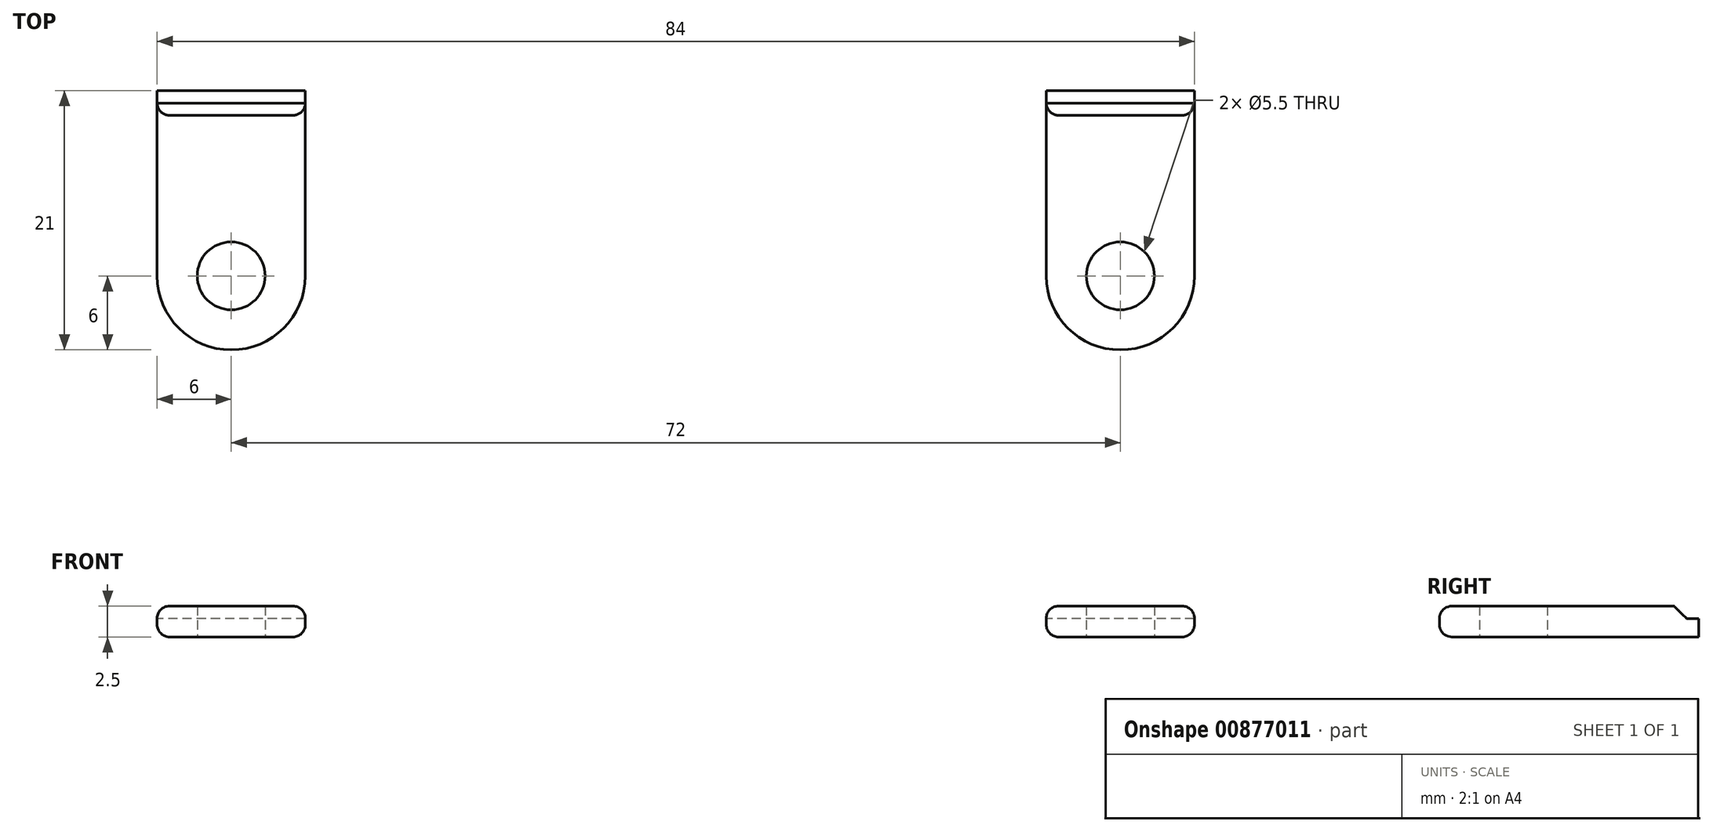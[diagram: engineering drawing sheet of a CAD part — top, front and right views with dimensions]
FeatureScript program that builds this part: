
annotation { "Feature Type Name" : "Feature", "Feature Type Description" : "" }
export const myFeature = defineFeature(function(context is Context, id is Id, definition is map)
    precondition{}
    {
        {
            var Q0;
            Q0=qCreatedBy(makeId("Top.planeOp"),FACE);
            var sketch = newSketch(context, id + "F0", { "sketchPlane" : qUnion([Q0])});
            skLineSegment(sketch, "E0", {"start": v(0, 0) * mm, "end": v(0, -15) * mm});
            skLineSegment(sketch, "E1", {"start": v(0, -15) * mm, "end": v(-12, -15) * mm, "construction": true});
            skLineSegment(sketch, "E2", {"start": v(-12, -15) * mm, "end": v(-12, 0) * mm});
            skLineSegment(sketch, "E3", {"start": v(-12, 0) * mm, "end": v(-72, 0) * mm});
            skLineSegment(sketch, "E4", {"start": v(-72, 0) * mm, "end": v(-72, -15) * mm});
            skLineSegment(sketch, "E5", {"start": v(-72, -15) * mm, "end": v(-84, -15) * mm, "construction": true});
            skLineSegment(sketch, "E6", {"start": v(-84, -15) * mm, "end": v(-84, 0) * mm});
            skLineSegment(sketch, "E7", {"start": v(-84, 0) * mm, "end": v(0, 0) * mm});
            skCircle(sketch, "E8", {"center": v(-78, -15) * mm, "radius": 6 * mm});
            skCircle(sketch, "E9", {"center": v(-6, -15) * mm, "radius": 6 * mm});
            skSolve(sketch);
        }
        {
            var Q0;
            {var subQ0=sQuery(id+"F0.wireOp",EDGE,"E8");var subQ1=makeQuery(id+"F0.imprint","INTERSECT",VERTEX,{"derivedFrom":[sQuery(id+"F0.wireOp",EDGE,"E4"),subQ0]});Q0=makeQuery(id+"F0.imprint","IMPRINT",FACE,{"disambiguationData":[TD([[makeQuery(id+"F0.imprint","IMPRINT",EDGE,{"disambiguationData":[TD([[subQ1,-1.0]])],"derivedFrom":subQ0}),1.0]])]});}
            var Q1;
            {var subQ2=sQuery(id+"F0.wireOp",EDGE,"E0");Q1=makeQuery(id+"F0.imprint","IMPRINT",FACE,{"disambiguationData":[TD([[makeQuery(id+"F0.imprint","IMPRINT",EDGE,{"derivedFrom":subQ2}),-1.0]])]});}
            var Q2;
            {var subQ0=sQuery(id+"F0.wireOp",EDGE,"E9");var subQ1=makeQuery(id+"F0.imprint","INTERSECT",VERTEX,{"derivedFrom":[sQuery(id+"F0.wireOp",EDGE,"E0"),subQ0]});Q2=makeQuery(id+"F0.imprint","IMPRINT",FACE,{"disambiguationData":[TD([[makeQuery(id+"F0.imprint","IMPRINT",EDGE,{"disambiguationData":[TD([[subQ1,-1.0]])],"derivedFrom":subQ0}),1.0]])]});}
            var Q3;
            {var subQ0=sQuery(id+"F0.wireOp",EDGE,"E4");Q3=makeQuery(id+"F0.imprint","IMPRINT",FACE,{"disambiguationData":[TD([[makeQuery(id+"F0.imprint","IMPRINT",EDGE,{"derivedFrom":subQ0}),-1.0]])]});}
            extrude(context, id + "F1", {"entities" : qUnion([Q0, Q1, Q2, Q3]), "depth" : 2.5 * mm, "offsetDistance" : 25.4 * mm});
        }
        {
            var Q0;
            Q0=sQuery(id+"F0.wireOp",VERTEX,"E8.center");
            var Q1;
            Q1=sQuery(id+"F0.wireOp",VERTEX,"E9.center");
            var Q2;
            Q2=makeQuery(id+"F1.opExtrude","SWEPT_BODY",BODY,{"disambiguationData":[OSD([sQuery(id+"F0.wireOp",EDGE,"E0"),sQuery(id+"F0.wireOp",EDGE,"E2"),sQuery(id+"F0.wireOp",EDGE,"E3"),sQuery(id+"F0.wireOp",EDGE,"E4"),sQuery(id+"F0.wireOp",EDGE,"E6"),sQuery(id+"F0.wireOp",EDGE,"E7"),sQuery(id+"F0.wireOp",EDGE,"E8"),sQuery(id+"F0.wireOp",EDGE,"E9")])]});
            hole(context, id + "F2", {"style" : HoleStyle.SIMPLE, "endStyle" : HoleEndStyle.THROUGH, "oppositeDirection" : true, "standardTappedOrClearance" : lookupTablePath({ "fit" : "Normal", "standard" : "ISO", "size" : "M5", "type" : "Clearance" }), "standardBlindInLast" : lookupTablePath({ "fit" : "Normal", "standard" : "ISO", "size" : "M5", "type" : "Clearance" }), "holeDiameter" : 5.5 * mm, "majorDiameter" : 6.35 * mm, "isTappedThrough" : true, "tappedDepth" : 12.7 * mm, "tapClearance" : 3, "startFromSketch" : true, "locations" : qUnion([Q0, Q1]), "scope" : qUnion([Q2])});
        }
        {
            var Q0;
            Q0=makeQuery(id+"F1.opExtrude","CAP_EDGE",EDGE,{"disambiguationData":[OSD([sQuery(id+"F0.wireOp",EDGE,"E6")])],"isStart":false});
            var Q1;
            Q1=makeQuery(id+"F1.opExtrude","CAP_EDGE",EDGE,{"disambiguationData":[OSD([sQuery(id+"F0.wireOp",EDGE,"E2")])],"isStart":false});
            var Q2;
            Q2=makeQuery(id+"F1.opExtrude","CAP_EDGE",EDGE,{"disambiguationData":[OSD([sQuery(id+"F0.wireOp",EDGE,"E6")])],"isStart":true});
            var Q3;
            Q3=makeQuery(id+"F1.opExtrude","CAP_EDGE",EDGE,{"disambiguationData":[OSD([sQuery(id+"F0.wireOp",EDGE,"E2")])],"isStart":true});
            fillet(context, id + "F3", {"entities" : qUnion([Q0, Q1, Q2, Q3]), "radius" : 1 * mm, "tangentPropagation" : true, "allowEdgeOverflow" : false});
        }
        {
            var Q0;
            Q0=makeQuery(id+"F1.opExtrude","SWEPT_FACE",FACE,{"disambiguationData":[OSD([sQuery(id+"F0.wireOp",EDGE,"E6")])]});
            var sketch = newSketch(context, id + "F4", { "sketchPlane" : qUnion([Q0])});
            skLineSegment(sketch, "E10", {"start": v(0, 1.5) * mm, "end": v(1, 1.5) * mm});
            skLineSegment(sketch, "E11", {"start": v(2, 2.5) * mm, "end": v(1, 1.5) * mm});
            skLineSegment(sketch, "E12", {"start": v(2, 2.5) * mm, "end": v(0, 2.5) * mm});
            skLineSegment(sketch, "E13", {"start": v(0, 2.5) * mm, "end": v(0, 1.5) * mm});
            skSolve(sketch);
        }
        {
            var Q0;
            Q0 = qSketchRegion(id + "F4", true);
            extrude(context, id + "F5", {"entities" : qUnion([Q0]), "operationType" : NewBodyOperationType.REMOVE, "endBound" : BoundingType.THROUGH_ALL, "oppositeDirection" : true, "depth" : 100 * mm, "offsetDistance" : 25 * mm});
        }
    });
